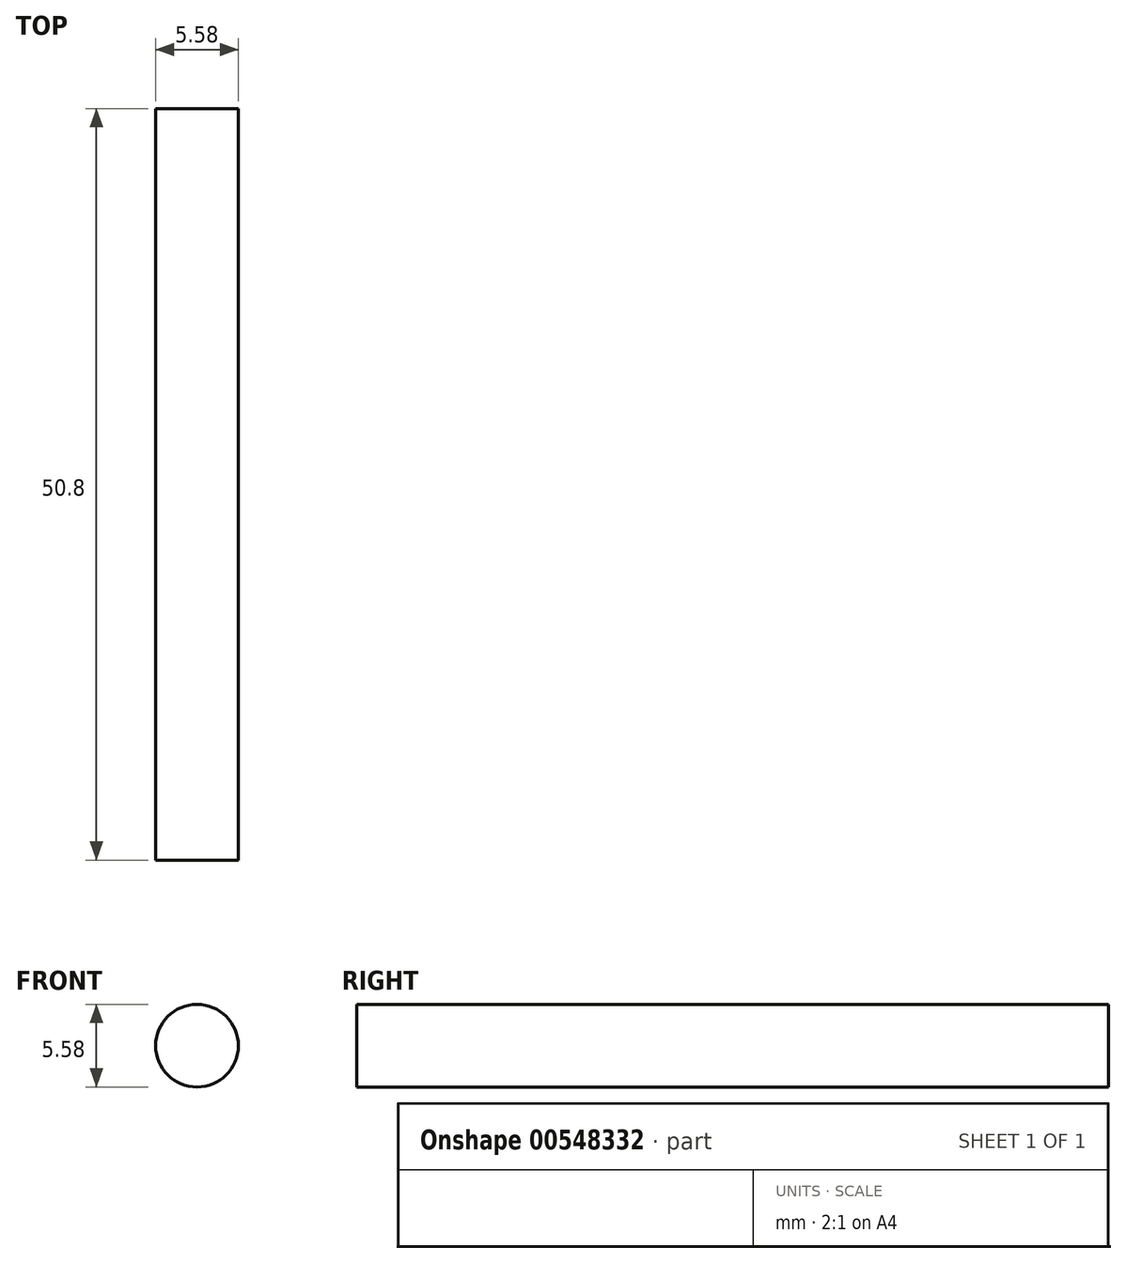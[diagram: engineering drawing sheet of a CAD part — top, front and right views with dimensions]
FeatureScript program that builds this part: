
annotation { "Feature Type Name" : "Feature", "Feature Type Description" : "" }
export const myFeature = defineFeature(function(context is Context, id is Id, definition is map)
    precondition{}
    {
        {
            var Q0;
            Q0=qCreatedBy(makeId("Front.planeOp"),FACE);
            var sketch = newSketch(context, id + "F0", { "sketchPlane" : qUnion([Q0])});
            skCircle(sketch, "E0", {"center": v(0, 0) * mm, "radius": 2.8 * mm});
            skSolve(sketch);
        }
        {
            var Q0;
            Q0 = qSketchRegion(id + "F0", true);
            extrude(context, id + "F1", {"entities" : qUnion([Q0]), "depth" : 50.8 * mm, "offsetDistance" : 25.4 * mm});
        }
    });
